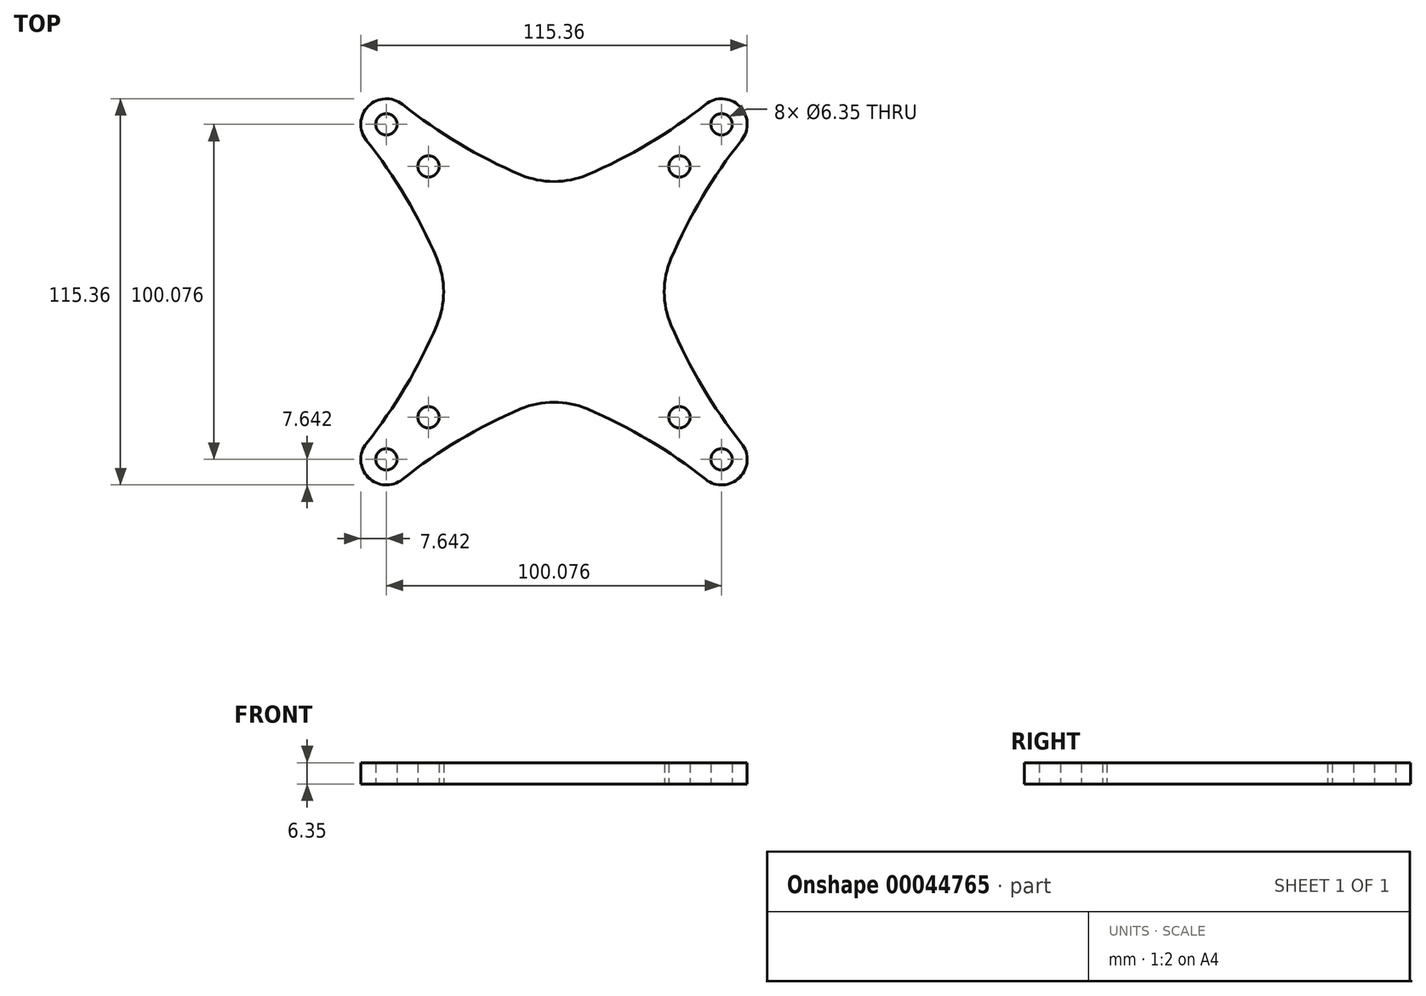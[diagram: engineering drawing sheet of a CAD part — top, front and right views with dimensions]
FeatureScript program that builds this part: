
annotation { "Feature Type Name" : "Feature", "Feature Type Description" : "" }
export const myFeature = defineFeature(function(context is Context, id is Id, definition is map)
    precondition{}
    {
        {
            var Q0;
            Q0=qCreatedBy(makeId("Top.planeOp"),FACE);
            var sketch = newSketch(context, id + "F0", { "sketchPlane" : qUnion([Q0])});
            skLineSegment(sketch, "E0.rect.bottom", {"start": v(-60.32, 60.33) * mm, "end": v(60.33, 60.33) * mm, "construction": true});
            skLineSegment(sketch, "E0.rect.top", {"start": v(-60.33, -60.32) * mm, "end": v(60.32, -60.32) * mm, "construction": true});
            skLineSegment(sketch, "E0.rect.left", {"start": v(-60.32, 60.33) * mm, "end": v(-60.33, -60.32) * mm, "construction": true});
            skLineSegment(sketch, "E0.rect.right", {"start": v(60.33, 60.33) * mm, "end": v(60.32, -60.32) * mm, "construction": true});
            skPoint(sketch, "E0.rect.middle", {"position": v(0, 0) * mm});
            skCircle(sketch, "E1", {"center": v(-50.04, 50.04) * mm, "radius": 3.18 * mm});
            skLineSegment(sketch, "E2", {"start": v(-50.04, 50.04) * mm, "end": v(0, 0) * mm, "construction": true});
            skCircle(sketch, "E3", {"center": v(-37.47, 37.46) * mm, "radius": 3.18 * mm});
            skCircle(sketch, "E4.MirrorC", {"center": v(-37.47, -37.46) * mm, "radius": 3.18 * mm});
            skCircle(sketch, "E5.MirrorC", {"center": v(-50.04, -50.04) * mm, "radius": 3.18 * mm});
            skLineSegment(sketch, "E6.MirrorCS", {"start": v(-50.04, -50.04) * mm, "end": v(0, 0) * mm, "construction": true});
            skCircle(sketch, "E7.MirrorC", {"center": v(37.47, 37.46) * mm, "radius": 3.18 * mm});
            skCircle(sketch, "E8.MirrorC", {"center": v(50.04, 50.04) * mm, "radius": 3.18 * mm});
            skLineSegment(sketch, "E9.MirrorCS", {"start": v(50.04, 50.04) * mm, "end": v(0, 0) * mm, "construction": true});
            skLineSegment(sketch, "E10.MirrorCS", {"start": v(50.04, -50.04) * mm, "end": v(0, 0) * mm, "construction": true});
            skCircle(sketch, "E11.MirrorC", {"center": v(37.47, -37.46) * mm, "radius": 3.18 * mm});
            skCircle(sketch, "E12.MirrorC", {"center": v(50.04, -50.04) * mm, "radius": 3.18 * mm});
            skArc(sketch, "E13", {"start": v(-45.28, 56.02) * mm, "mid": v(-55.44, 55.44) * mm, "end": v(-56.02, 45.28) * mm});
            skArc(sketch, "E14", {"start": v(-34.97, 9.93) * mm, "mid": v(-44.3, 28.32) * mm, "end": v(-56.02, 45.28) * mm});
            skArc(sketch, "E15.MirrorCS", {"start": v(-9.93, 34.97) * mm, "mid": v(-28.32, 44.3) * mm, "end": v(-45.28, 56.02) * mm});
            skArc(sketch, "E16.1.0", {"start": v(-34.97, -9.93) * mm, "mid": v(-44.3, -28.32) * mm, "end": v(-56.02, -45.28) * mm});
            skArc(sketch, "E16.1.1", {"start": v(-9.93, -34.97) * mm, "mid": v(-28.32, -44.3) * mm, "end": v(-45.28, -56.02) * mm});
            skArc(sketch, "E16.1.2", {"start": v(-56.02, -45.28) * mm, "mid": v(-55.44, -55.44) * mm, "end": v(-45.28, -56.02) * mm});
            skArc(sketch, "E16.2.0", {"start": v(9.93, -34.97) * mm, "mid": v(28.32, -44.3) * mm, "end": v(45.28, -56.02) * mm});
            skArc(sketch, "E16.2.1", {"start": v(34.97, -9.93) * mm, "mid": v(44.3, -28.32) * mm, "end": v(56.02, -45.28) * mm});
            skArc(sketch, "E16.2.2", {"start": v(45.28, -56.02) * mm, "mid": v(55.44, -55.44) * mm, "end": v(56.02, -45.28) * mm});
            skArc(sketch, "E16.3.0", {"start": v(34.97, 9.93) * mm, "mid": v(44.3, 28.32) * mm, "end": v(56.02, 45.28) * mm});
            skArc(sketch, "E16.3.1", {"start": v(9.93, 34.97) * mm, "mid": v(28.32, 44.3) * mm, "end": v(45.28, 56.02) * mm});
            skArc(sketch, "E16.3.2", {"start": v(56.02, 45.28) * mm, "mid": v(55.44, 55.44) * mm, "end": v(45.28, 56.02) * mm});
            skPoint(sketch, "E17.visualSharp", {"position": v(-31.15, 0) * mm});
            skArc(sketch, "E17.filletArc", {"start": v(-34.97, -9.93) * mm, "mid": v(-32.95, 0) * mm, "end": v(-34.97, 9.93) * mm});
            skPoint(sketch, "E18.visualSharp", {"position": v(0, 31.15) * mm});
            skArc(sketch, "E18.filletArc", {"start": v(-9.93, 34.97) * mm, "mid": v(0, 32.95) * mm, "end": v(9.93, 34.97) * mm});
            skPoint(sketch, "E19.visualSharp", {"position": v(31.15, 0) * mm});
            skArc(sketch, "E19.filletArc", {"start": v(34.97, 9.93) * mm, "mid": v(32.95, 0) * mm, "end": v(34.97, -9.93) * mm});
            skPoint(sketch, "E20.visualSharp", {"position": v(0, -31.15) * mm});
            skArc(sketch, "E20.filletArc", {"start": v(9.93, -34.97) * mm, "mid": v(0, -32.95) * mm, "end": v(-9.93, -34.97) * mm});
            skCircle(sketch, "E21", {"center": v(0, 0) * mm, "radius": 23.14 * mm, "construction": true});
            skSolve(sketch);
        }
        {
            var Q0;
            Q0=makeQuery(id+"F0.imprint","IMPRINT",FACE,{"disambiguationData":[TD([[makeQuery(id+"F0.imprint","IMPRINT",EDGE,{"derivedFrom":sQuery(id+"F0.wireOp",EDGE,"E1")}),-1.0]])]});
            extrude(context, id + "F1", {"entities" : qUnion([Q0]), "depth" : 6.35 * mm});
        }
    });
